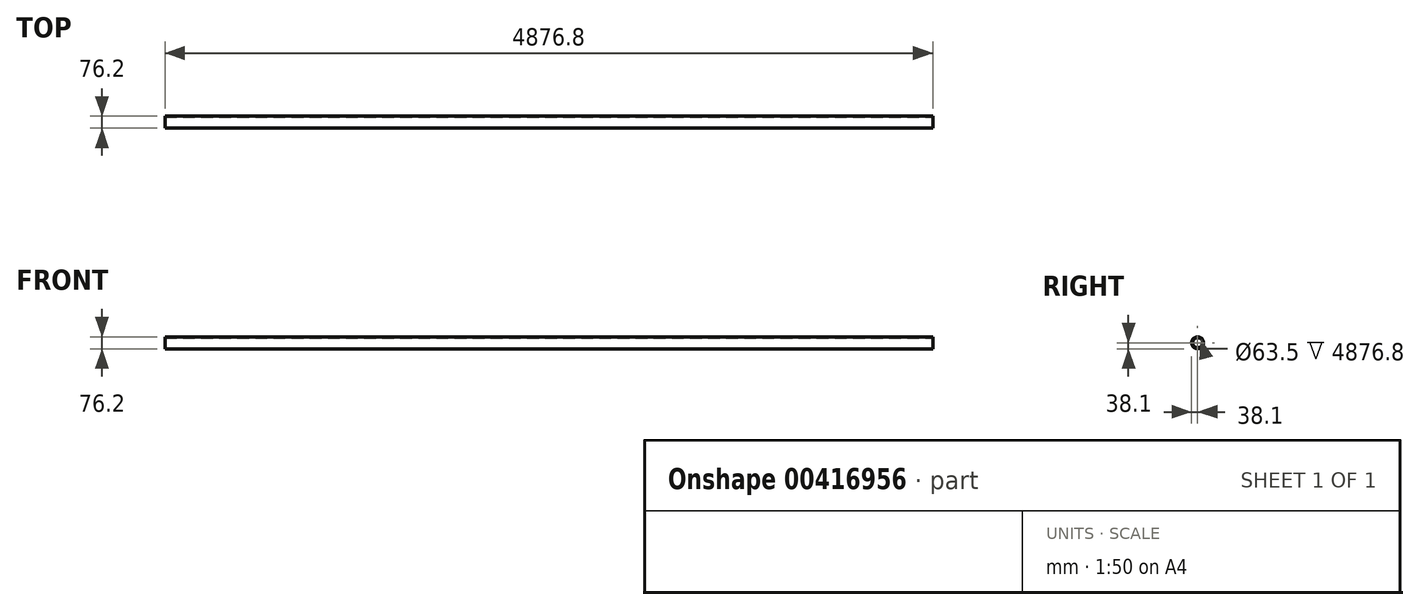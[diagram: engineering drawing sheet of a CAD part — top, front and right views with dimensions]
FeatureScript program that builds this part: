
annotation { "Feature Type Name" : "Feature", "Feature Type Description" : "" }
export const myFeature = defineFeature(function(context is Context, id is Id, definition is map)
    precondition{}
    {
        {
            var Q0;
            Q0=qCreatedBy(makeId("Right.planeOp"),FACE);
            var sketch = newSketch(context, id + "F0", { "sketchPlane" : qUnion([Q0])});
            skCircle(sketch, "E0", {"center": v(2438.4, 0) * mm, "radius": 38.1 * mm});
            skLineSegment(sketch, "E1", {"start": v(-7.6, 0) * mm, "end": v(58.89, 0) * mm});
            skLineSegment(sketch, "E2", {"start": v(0, -25.67) * mm, "end": v(0, 40.82) * mm});
            skLineSegment(sketch, "E3", {"start": v(-12.33, 0) * mm, "end": v(115.57, 0) * mm});
            skCircle(sketch, "E4", {"center": v(-472.96, -360.48) * mm, "radius": 334 * mm});
            skSolve(sketch);
        }
        {
            var Q0;
            Q0=makeQuery(id+"F0.imprint","IMPRINT",FACE,{"disambiguationData":[TD([[makeQuery(id+"F0.imprint","IMPRINT",EDGE,{"derivedFrom":sQuery(id+"F0.wireOp",EDGE,"E0")}),1.0]])]});
            extrude(context, id + "F1", {"entities" : qUnion([Q0]), "endBound" : BoundingType.SYMMETRIC, "oppositeDirection" : true, "depth" : 4876.8 * mm});
        }
        {
            var Q0;
            Q0=makeQuery(id+"F1.opExtrude","CAP_FACE",FACE,{"disambiguationData":[OSD([sQuery(id+"F0.wireOp",EDGE,"E0")])],"isStart":false});
            var Q1;
            Q1=makeQuery(id+"F1.opExtrude","CAP_FACE",FACE,{"disambiguationData":[OSD([sQuery(id+"F0.wireOp",EDGE,"E0")])],"isStart":true});
            shell(context, id + "F2", {"entities" : qUnion([Q0, Q1]), "thickness" : 6.35 * mm});
        }
    });
